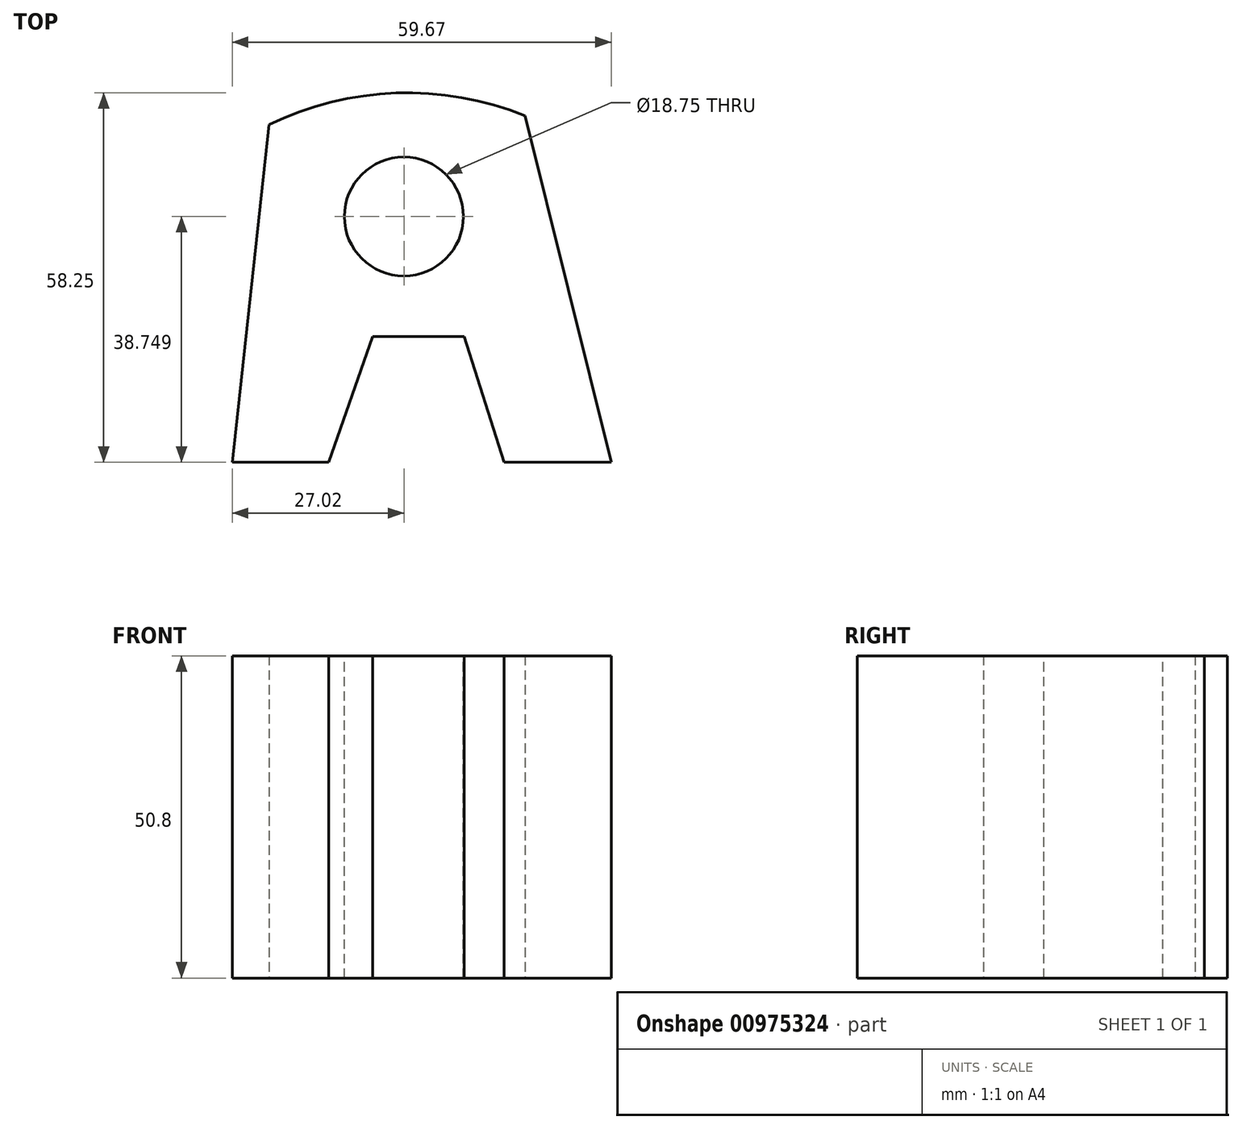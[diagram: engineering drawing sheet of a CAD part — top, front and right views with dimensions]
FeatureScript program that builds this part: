
annotation { "Feature Type Name" : "Feature", "Feature Type Description" : "" }
export const myFeature = defineFeature(function(context is Context, id is Id, definition is map)
    precondition{}
    {
        {
            var Q0;
            Q0=qCreatedBy(makeId("Top.planeOp"),FACE);
            var sketch = newSketch(context, id + "F0", { "sketchPlane" : qUnion([Q0])});
            skArc(sketch, "E0", {"start": v(19.06, 48.67) * mm, "mid": v(-1.23, 52.24) * mm, "end": v(-21.22, 47.23) * mm});
            skLineSegment(sketch, "E1", {"start": v(-21.22, 47.23) * mm, "end": v(-27.02, -5.98) * mm});
            skLineSegment(sketch, "E2", {"start": v(19.06, 48.67) * mm, "end": v(32.65, -5.98) * mm});
            skLineSegment(sketch, "E3", {"start": v(-27.02, -5.98) * mm, "end": v(-11.84, -5.98) * mm});
            skLineSegment(sketch, "E4", {"start": v(-11.84, -5.98) * mm, "end": v(-4.9, 13.87) * mm});
            skLineSegment(sketch, "E5", {"start": v(-4.9, 13.87) * mm, "end": v(9.5, 13.87) * mm});
            skLineSegment(sketch, "E6", {"start": v(9.5, 13.87) * mm, "end": v(15.77, -5.98) * mm});
            skLineSegment(sketch, "E7", {"start": v(15.77, -5.98) * mm, "end": v(32.65, -5.98) * mm});
            skPoint(sketch, "E8", {"position": v(0, 52.27) * mm});
            skPoint(sketch, "E9", {"position": v(49.4, 46.4) * mm});
            skSolve(sketch);
        }
        {
            var Q0;
            Q0 = qSketchRegion(id + "F0", true);
            extrude(context, id + "F1", {"entities" : qUnion([Q0]), "depth" : 25.4 * mm, "offsetDistance" : 25.4 * mm});
        }
        {
            var Q0;
            Q0 = qSketchRegion(id + "F0", true);
            var Q1;
            Q1=makeQuery(id+"F1.opExtrude","CAP_FACE",FACE,{"disambiguationData":[OSD([sQuery(id+"F0.wireOp",EDGE,"E0"),sQuery(id+"F0.wireOp",EDGE,"E1"),sQuery(id+"F0.wireOp",EDGE,"E2"),sQuery(id+"F0.wireOp",EDGE,"E3"),sQuery(id+"F0.wireOp",EDGE,"E4"),sQuery(id+"F0.wireOp",EDGE,"E5"),sQuery(id+"F0.wireOp",EDGE,"E6"),sQuery(id+"F0.wireOp",EDGE,"E7")])],"isStart":false});
            extrude(context, id + "F2", {"entities" : qUnion([Q0, Q1]), "operationType" : NewBodyOperationType.ADD, "endBound" : BoundingType.SYMMETRIC, "depth" : 25.4 * mm, "offsetDistance" : 25.4 * mm});
        }
        {
            var Q0;
            {var subQ0=sQuery(id+"F0.wireOp",EDGE,"E7");var subQ1=sQuery(id+"F0.wireOp",EDGE,"E6");var subQ2=sQuery(id+"F0.wireOp",EDGE,"E5");var subQ3=sQuery(id+"F0.wireOp",EDGE,"E4");var subQ4=sQuery(id+"F0.wireOp",EDGE,"E3");var subQ5=sQuery(id+"F0.wireOp",EDGE,"E2");var subQ6=sQuery(id+"F0.wireOp",EDGE,"E1");var subQ7=sQuery(id+"F0.wireOp",EDGE,"E0");Q0=makeQuery(id+"F2.opExtrude","CAP_FACE",FACE,{"disambiguationData":[OSD([subQ7,subQ6,subQ5,subQ4,subQ3,subQ2,subQ1,subQ0]),TDD([makeQuery(id+"F1.opExtrude","CAP_FACE",FACE,{"disambiguationData":[OSD([subQ7,subQ6,subQ5,subQ4,subQ3,subQ2,subQ1,subQ0])],"isStart":false})])],"isStart":false});}
            var sketch = newSketch(context, id + "F3", { "sketchPlane" : qUnion([Q0])});
            skCircle(sketch, "E10", {"center": v(0, 32.77) * mm, "radius": 9.38 * mm});
            skSolve(sketch);
        }
        {
            var Q0;
            Q0=makeQuery(id+"F3.imprint","IMPRINT",FACE,{"disambiguationData":[TD([[makeQuery(id+"F3.imprint","IMPRINT",EDGE,{"derivedFrom":sQuery(id+"F3.wireOp",EDGE,"E10")}),1.0]])]});
            extrude(context, id + "F4", {"entities" : qUnion([Q0]), "operationType" : NewBodyOperationType.REMOVE, "endBound" : BoundingType.SYMMETRIC, "oppositeDirection" : true, "depth" : 25.4 * mm, "offsetDistance" : 25.4 * mm});
        }
        {
            var Q0;
            Q0=makeQuery(id+"F4.boolean.opBoolean","COPY",FACE,{"derivedFrom":makeQuery(id+"F4.opExtrude","CAP_FACE",FACE,{"disambiguationData":[OSD([sQuery(id+"F3.wireOp",EDGE,"E10")])],"isStart":false})});
            extrude(context, id + "F5", {"entities" : qUnion([Q0]), "operationType" : NewBodyOperationType.REMOVE, "endBound" : BoundingType.THROUGH_ALL, "oppositeDirection" : true, "depth" : 25.4 * mm, "offsetDistance" : 25.4 * mm});
        }
    });
